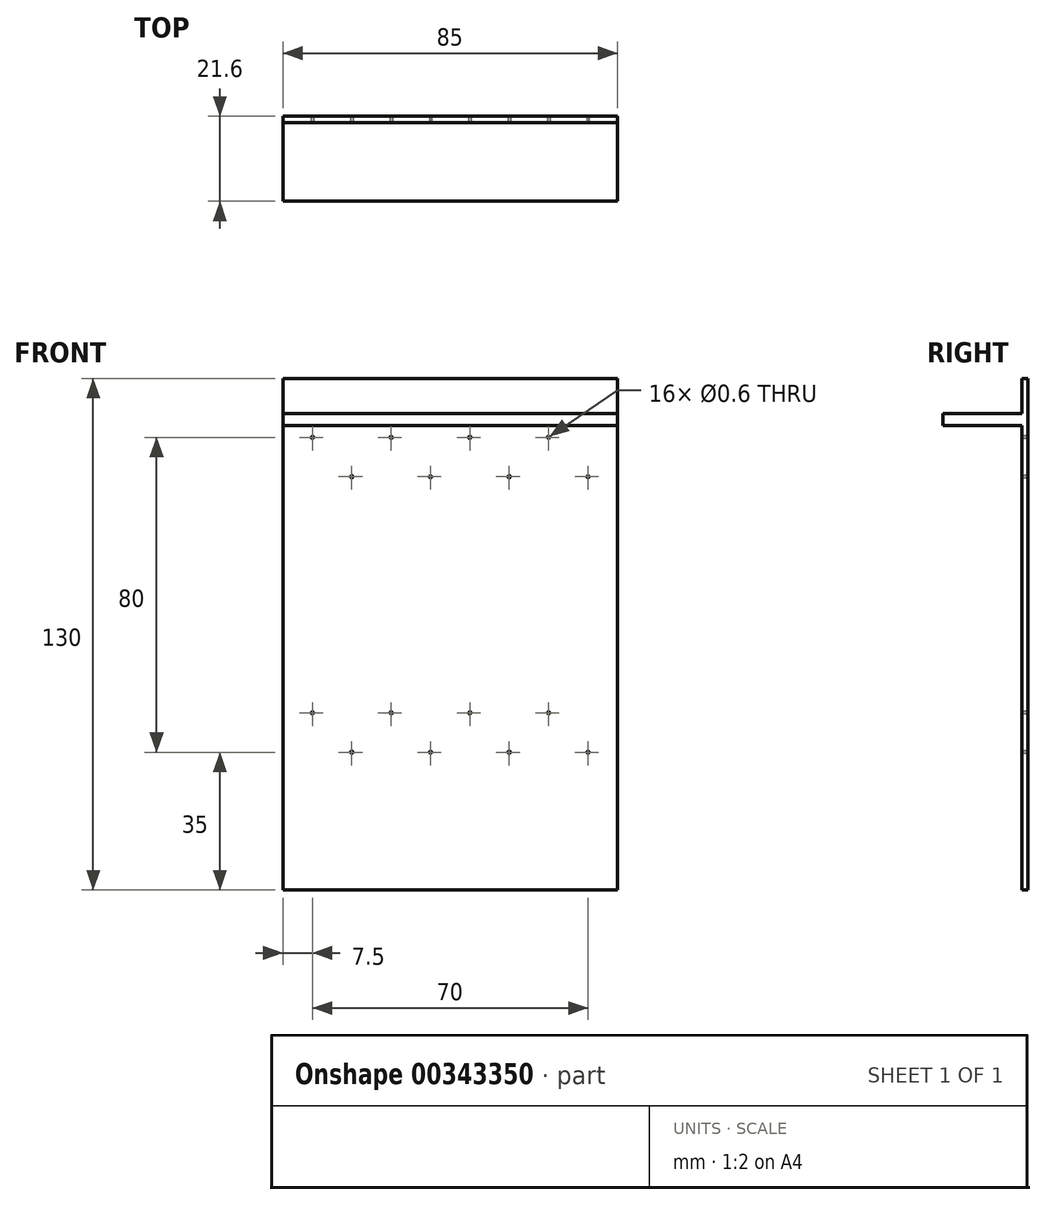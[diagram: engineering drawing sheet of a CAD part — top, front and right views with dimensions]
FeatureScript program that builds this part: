
annotation { "Feature Type Name" : "Feature", "Feature Type Description" : "" }
export const myFeature = defineFeature(function(context is Context, id is Id, definition is map)
    precondition{}
    {
        {
            var Q0;
            Q0=qCreatedBy(makeId("Front.planeOp"),FACE);
            var sketch = newSketch(context, id + "F0", { "sketchPlane" : qUnion([Q0])});
            skLineSegment(sketch, "E0.bottom", {"start": v(42.5, 65) * mm, "end": v(-42.5, 65) * mm});
            skLineSegment(sketch, "E0.top", {"start": v(42.5, -65) * mm, "end": v(-42.5, -65) * mm});
            skLineSegment(sketch, "E0.left", {"start": v(42.5, 65) * mm, "end": v(42.5, -65) * mm});
            skLineSegment(sketch, "E0.right", {"start": v(-42.5, 65) * mm, "end": v(-42.5, -65) * mm});
            skPoint(sketch, "E0.middle", {"position": v(0, 0) * mm});
            skCircle(sketch, "E1", {"center": v(-35, 50) * mm, "radius": 0.3 * mm});
            skCircle(sketch, "E2", {"center": v(-25, 40) * mm, "radius": 0.3 * mm});
            skCircle(sketch, "E3", {"center": v(-15, 50) * mm, "radius": 0.3 * mm});
            skCircle(sketch, "E4", {"center": v(-5, 40) * mm, "radius": 0.3 * mm});
            skCircle(sketch, "E5", {"center": v(5, 50) * mm, "radius": 0.3 * mm});
            skCircle(sketch, "E6", {"center": v(15, 40) * mm, "radius": 0.3 * mm});
            skCircle(sketch, "E7", {"center": v(25, 50) * mm, "radius": 0.3 * mm});
            skCircle(sketch, "E8", {"center": v(35, 40) * mm, "radius": 0.3 * mm});
            skCircle(sketch, "E9", {"center": v(-35, -20) * mm, "radius": 0.3 * mm});
            skCircle(sketch, "E10", {"center": v(-25, -30) * mm, "radius": 0.3 * mm});
            skCircle(sketch, "E11", {"center": v(-15, -20) * mm, "radius": 0.3 * mm});
            skCircle(sketch, "E12", {"center": v(-5, -30) * mm, "radius": 0.3 * mm});
            skCircle(sketch, "E13", {"center": v(5, -20) * mm, "radius": 0.3 * mm});
            skCircle(sketch, "E14", {"center": v(15, -30) * mm, "radius": 0.3 * mm});
            skCircle(sketch, "E15", {"center": v(25, -20) * mm, "radius": 0.3 * mm});
            skCircle(sketch, "E16", {"center": v(35, -30) * mm, "radius": 0.3 * mm});
            skLineSegment(sketch, "E17.bottom", {"start": v(-42.5, 53) * mm, "end": v(42.5, 53) * mm});
            skLineSegment(sketch, "E17.top", {"start": v(-42.5, 56) * mm, "end": v(42.5, 56) * mm});
            skLineSegment(sketch, "E17.left", {"start": v(-42.5, 53) * mm, "end": v(-42.5, 56) * mm});
            skLineSegment(sketch, "E17.right", {"start": v(42.5, 53) * mm, "end": v(42.5, 56) * mm});
            skSolve(sketch);
        }
        {
            var Q0;
            Q0 = qSketchRegion(id + "F0", true);
            extrude(context, id + "F1", {"entities" : qUnion([Q0]), "depth" : 0 * mm, "hasSecondDirection" : true, "secondDirectionOppositeDirection" : true, "secondDirectionDepth" : 1.6 * mm});
        }
        {
            var Q0;
            Q0=makeQuery(id+"F0.imprint","IMPRINT",FACE,{"disambiguationData":[TD([[makeQuery(id+"F0.imprint","IMPRINT",EDGE,{"derivedFrom":sQuery(id+"F0.wireOp",EDGE,"E17.bottom")}),1.0]])]});
            extrude(context, id + "F2", {"entities" : qUnion([Q0]), "operationType" : NewBodyOperationType.ADD, "depth" : 20 * mm});
        }
    });
